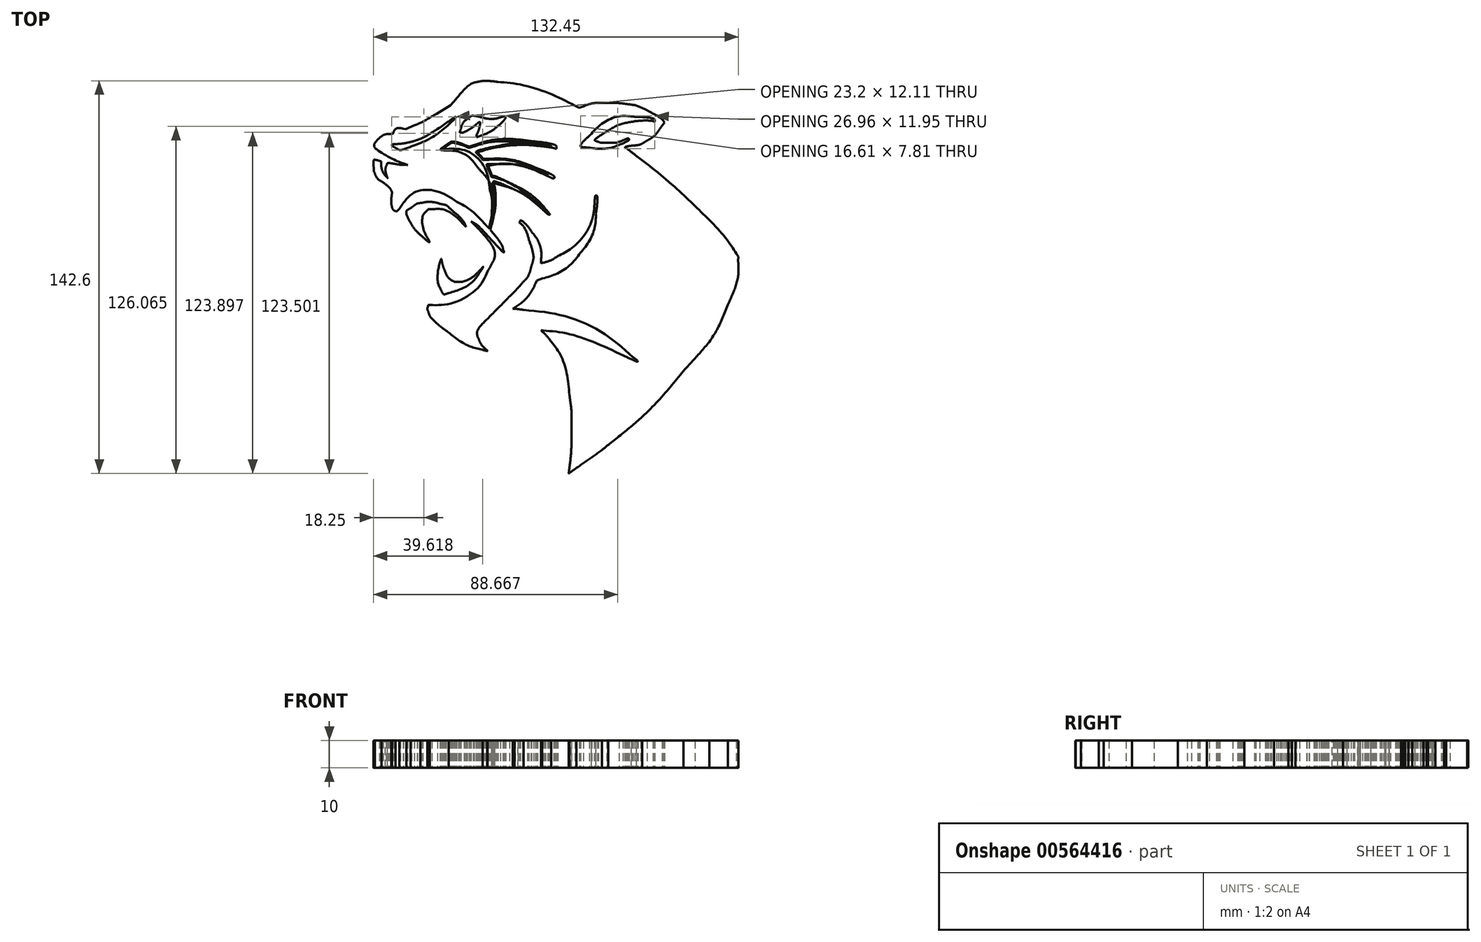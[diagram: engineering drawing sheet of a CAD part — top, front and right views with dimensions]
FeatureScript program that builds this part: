
annotation { "Feature Type Name" : "Feature", "Feature Type Description" : "" }
export const myFeature = defineFeature(function(context is Context, id is Id, definition is map)
    precondition{}
    {
        {
            var Q0;
            Q0=qCreatedBy(makeId("Top.planeOp"),FACE);
            var sketch = newSketch(context, id + "F0", { "sketchPlane" : qUnion([Q0])});
            skFitSpline(sketch, "E0", {"points": [v(4.12, -71.12) * mm, v(4.12, -70.9) * mm, v(4.21, -70) * mm, v(4.32, -69.1) * mm]});
            skFitSpline(sketch, "E1", {"points": [v(4.32, -69.1) * mm, v(5.26, -61.65) * mm, v(5.42, -52.29) * mm, v(4.74, -45.44) * mm]});
            skFitSpline(sketch, "E2", {"points": [v(4.74, -45.44) * mm, v(3.83, -36.4) * mm, v(1.7, -29.31) * mm, v(-1.62, -24.22) * mm]});
            skFitSpline(sketch, "E3", {"points": [v(-1.62, -24.22) * mm, v(-2.63, -22.67) * mm, v(-4.78, -20.17) * mm, v(-5.73, -19.43) * mm]});
            skFitSpline(sketch, "E4", {"points": [v(-5.73, -19.43) * mm, v(-6.02, -19.21) * mm, v(-6.25, -18.9) * mm, v(-6.25, -18.75) * mm]});
            skFitSpline(sketch, "E5", {"points": [v(-6.25, -18.75) * mm, v(-6.25, -18.44) * mm, v(-6.19, -18.44) * mm, v(-2.93, -18.9) * mm]});
            skFitSpline(sketch, "E6", {"points": [v(-2.93, -18.9) * mm, v(4, -19.85) * mm, v(14.69, -23.35) * mm, v(25.2, -28.1) * mm]});
            skFitSpline(sketch, "E7", {"points": [v(25.2, -28.1) * mm, v(26.49, -28.69) * mm, v(27.64, -29.2) * mm, v(27.75, -29.25) * mm]});
            skFitSpline(sketch, "E8", {"points": [v(27.75, -29.25) * mm, v(28.18, -29.42) * mm, v(23.73, -26.1) * mm, v(21.96, -24.93) * mm]});
            skFitSpline(sketch, "E9", {"points": [v(21.96, -24.93) * mm, v(11.21, -17.82) * mm, v(-2.37, -12.86) * mm, v(-14.52, -11.6) * mm]});
            skFitSpline(sketch, "E10", {"points": [v(-14.52, -11.6) * mm, v(-16.71, -11.38) * mm, v(-16.9, -11.24) * mm, v(-15.82, -10.6) * mm]});
            skFitSpline(sketch, "E11", {"points": [v(-15.82, -10.6) * mm, v(-13.27, -9.1) * mm, v(-9.35, -4.61) * mm, v(-7.78, -1.4) * mm]});
            skFitSpline(sketch, "E12", {"points": [v(-7.78, -1.4) * mm, v(-7.39, -0.6) * mm, v(-7.26, -0.46) * mm, v(-6.75, -0.31) * mm]});
            skFitSpline(sketch, "E13", {"points": [v(-6.75, -0.31) * mm, v(-4.24, 0.42) * mm, v(-0.38, 2.42) * mm, v(1.98, 4.23) * mm]});
            skFitSpline(sketch, "E14", {"points": [v(1.98, 4.23) * mm, v(9.16, 9.74) * mm, v(13.82, 18.08) * mm, v(14.15, 26.05) * mm]});
            skFitSpline(sketch, "E15", {"points": [v(13.87, 26.2) * mm, v(12.03, 18.53) * mm, v(6.27, 10.76) * mm, v(-0.37, 7) * mm]});
            skFitSpline(sketch, "E16", {"points": [v(-0.37, 7) * mm, v(-1.97, 6.1) * mm, v(-4.01, 5.3) * mm, v(-5.09, 5.16) * mm]});
            skLineSegment(sketch, "E17", {"start": v(14.15, 26.05) * mm, "end": v(14.22, 27.64) * mm});
            skLineSegment(sketch, "E18", {"start": v(14.22, 27.64) * mm, "end": v(13.87, 26.2) * mm});
            skFitSpline(sketch, "E19", {"points": [v(-5.83, 5.76) * mm, v(-5.83, 9.94) * mm, v(-7.3, 14.16) * mm, v(-9.82, 17.24) * mm]});
            skFitSpline(sketch, "E20", {"points": [v(-9.82, 17.24) * mm, v(-10.64, 18.24) * mm, v(-11.89, 19.44) * mm, v(-12.11, 19.44) * mm]});
            skFitSpline(sketch, "E21", {"points": [v(-12.11, 19.44) * mm, v(-12.17, 19.44) * mm, v(-12, 19.13) * mm, v(-11.74, 18.76) * mm]});
            skFitSpline(sketch, "E22", {"points": [v(-11.74, 18.76) * mm, v(-9.25, 15.2) * mm, v(-8.15, 8.63) * mm, v(-9.24, 3.9) * mm]});
            skFitSpline(sketch, "E23", {"points": [v(-9.24, 3.9) * mm, v(-9.57, 2.5) * mm, v(-10.53, 0.23) * mm, v(-11.3, -0.93) * mm]});
            skFitSpline(sketch, "E24", {"points": [v(-11.3, -0.93) * mm, v(-12.03, -2.05) * mm, v(-14.6, -4.79) * mm, v(-20.43, -10.68) * mm]});
            skFitSpline(sketch, "E25", {"points": [v(-20.43, -10.68) * mm, v(-25.1, -15.4) * mm, v(-27.6, -18.05) * mm, v(-27.91, -18.6) * mm]});
            skFitSpline(sketch, "E26", {"points": [v(-27.91, -18.6) * mm, v(-28.04, -18.82) * mm, v(-28.17, -19.43) * mm, v(-28.2, -20.02) * mm]});
            skFitSpline(sketch, "E27", {"points": [v(-28.2, -20.02) * mm, v(-28.25, -20.95) * mm, v(-28.2, -21.15) * mm, v(-27.74, -22.24) * mm]});
            skFitSpline(sketch, "E28", {"points": [v(-27.74, -22.24) * mm, v(-27.16, -23.6) * mm, v(-25.99, -25.08) * mm, v(-24.73, -26.04) * mm]});
            skFitSpline(sketch, "E29", {"points": [v(-24.73, -26.04) * mm, v(-24.3, -26.37) * mm, v(-23.94, -26.7) * mm, v(-23.94, -26.78) * mm]});
            skFitSpline(sketch, "E30", {"points": [v(-23.94, -26.78) * mm, v(-23.94, -27.37) * mm, v(-28.38, -26.2) * mm, v(-31.6, -24.76) * mm]});
            skFitSpline(sketch, "E31", {"points": [v(-31.6, -24.76) * mm, v(-33.32, -24) * mm, v(-36.75, -22.01) * mm, v(-38.31, -20.87) * mm]});
            skFitSpline(sketch, "E32", {"points": [v(-38.31, -20.87) * mm, v(-42.29, -17.96) * mm, v(-45.58, -14.42) * mm, v(-46.56, -12.02) * mm]});
            skFitSpline(sketch, "E33", {"points": [v(-46.56, -12.02) * mm, v(-46.91, -11.14) * mm, v(-47, -9.7) * mm, v(-46.7, -9.43) * mm]});
            skFitSpline(sketch, "E34", {"points": [v(-46.7, -9.43) * mm, v(-46.61, -9.35) * mm, v(-45.91, -9.24) * mm, v(-45.15, -9.2) * mm]});
            skFitSpline(sketch, "E35", {"points": [v(-45.15, -9.2) * mm, v(-40.65, -8.93) * mm, v(-34.12, -5.97) * mm, v(-29.58, -2.15) * mm]});
            skFitSpline(sketch, "E36", {"points": [v(-29.58, -2.15) * mm, v(-28.1, -0.9) * mm, v(-26.11, 1.39) * mm, v(-25.28, 2.8) * mm]});
            skFitSpline(sketch, "E37", {"points": [v(-25.28, 2.8) * mm, v(-22.36, 7.75) * mm, v(-24.01, 12.95) * mm, v(-30.64, 19.72) * mm]});
            skFitSpline(sketch, "E38", {"points": [v(-30.64, 19.72) * mm, v(-31.44, 20.54) * mm, v(-31.7, 20.9) * mm, v(-31.6, 21.03) * mm]});
            skFitSpline(sketch, "E39", {"points": [v(-31.6, 21.03) * mm, v(-31.38, 21.28) * mm, v(-30.28, 20.82) * mm, v(-29.2, 20) * mm]});
            skFitSpline(sketch, "E40", {"points": [v(-29.2, 20) * mm, v(-28, 19.11) * mm, v(-26.82, 17.97) * mm, v(-23.58, 14.52) * mm]});
            skFitSpline(sketch, "E41", {"points": [v(-23.58, 14.52) * mm, v(-22.08, 12.93) * mm, v(-20.62, 11.4) * mm, v(-20.32, 11.13) * mm]});
            skLineSegment(sketch, "E42", {"start": v(-5.09, 5.16) * mm, "end": v(-5.83, 5.06) * mm});
            skLineSegment(sketch, "E43", {"start": v(-5.83, 5.06) * mm, "end": v(-5.83, 5.76) * mm});
            skFitSpline(sketch, "E44", {"points": [v(-20.21, 11.5) * mm, v(-21.27, 13.58) * mm, v(-23.88, 16.98) * mm, v(-26.22, 19.32) * mm]});
            skFitSpline(sketch, "E45", {"points": [v(-26.22, 19.32) * mm, v(-27.27, 20.37) * mm, v(-29.86, 22.55) * mm, v(-31.29, 23.58) * mm]});
            skFitSpline(sketch, "E46", {"points": [v(-31.29, 23.58) * mm, v(-41.27, 30.8) * mm, v(-51.02, 31.4) * mm, v(-57.07, 25.13) * mm]});
            skFitSpline(sketch, "E47", {"points": [v(-57.07, 25.13) * mm, v(-57.88, 24.29) * mm, v(-57.96, 24.24) * mm, v(-58.38, 24.38) * mm]});
            skFitSpline(sketch, "E48", {"points": [v(-58.38, 24.38) * mm, v(-58.96, 24.57) * mm, v(-59.54, 25.3) * mm, v(-59.73, 26.08) * mm]});
            skFitSpline(sketch, "E49", {"points": [v(-59.73, 26.08) * mm, v(-59.9, 26.77) * mm, v(-59.9, 29.14) * mm, v(-59.75, 30.4) * mm]});
            skFitSpline(sketch, "E50", {"points": [v(-59.75, 30.4) * mm, v(-59.67, 31.05) * mm, v(-59.7, 31.33) * mm, v(-59.88, 31.67) * mm]});
            skFitSpline(sketch, "E51", {"points": [v(-59.88, 31.67) * mm, v(-60.31, 32.5) * mm, v(-62.06, 34.15) * mm, v(-63.53, 35.12) * mm]});
            skFitSpline(sketch, "E52", {"points": [v(-63.53, 35.12) * mm, v(-64.59, 35.83) * mm, v(-65.36, 36.75) * mm, v(-65.84, 37.88) * mm]});
            skFitSpline(sketch, "E53", {"points": [v(-65.84, 37.88) * mm, v(-66.21, 38.74) * mm, v(-66.3, 39.14) * mm, v(-66.34, 40.28) * mm]});
            skFitSpline(sketch, "E54", {"points": [v(-66.34, 40.28) * mm, v(-66.4, 41.8) * mm, v(-66.2, 43.01) * mm, v(-65.88, 43.01) * mm]});
            skFitSpline(sketch, "E55", {"points": [v(-65.88, 43.01) * mm, v(-65.77, 43.01) * mm, v(-65.22, 42.9) * mm, v(-64.65, 42.75) * mm]});
            skLineSegment(sketch, "E56", {"start": v(-20.32, 11.13) * mm, "end": v(-19.78, 10.64) * mm});
            skLineSegment(sketch, "E57", {"start": v(-19.78, 10.64) * mm, "end": v(-20.21, 11.5) * mm});
            skFitSpline(sketch, "E58", {"points": [v(-63.6, 41.83) * mm, v(-63.6, 40.8) * mm, v(-63.23, 39.05) * mm, v(-62.86, 38.34) * mm]});
            skFitSpline(sketch, "E59", {"points": [v(-62.86, 38.34) * mm, v(-62.67, 37.97) * mm, v(-62.22, 37.35) * mm, v(-61.86, 36.96) * mm]});
            skFitSpline(sketch, "E60", {"points": [v(-61.86, 36.96) * mm, v(-61.5, 36.57) * mm, v(-61.27, 36.35) * mm, v(-61.35, 36.48) * mm]});
            skFitSpline(sketch, "E61", {"points": [v(-61.35, 36.48) * mm, v(-61.44, 36.61) * mm, v(-61.61, 37.15) * mm, v(-61.74, 37.67) * mm]});
            skFitSpline(sketch, "E62", {"points": [v(-61.74, 37.67) * mm, v(-62.03, 38.8) * mm, v(-61.96, 40.31) * mm, v(-61.58, 41.2) * mm]});
            skFitSpline(sketch, "E63", {"points": [v(-61.58, 41.2) * mm, v(-61.34, 41.77) * mm, v(-61.28, 41.82) * mm, v(-60.77, 41.8) * mm]});
            skFitSpline(sketch, "E64", {"points": [v(-60.77, 41.8) * mm, v(-60.47, 41.79) * mm, v(-59.54, 41.66) * mm, v(-58.7, 41.51) * mm]});
            skFitSpline(sketch, "E65", {"points": [v(-58.7, 41.51) * mm, v(-57.87, 41.37) * mm, v(-56.47, 41.2) * mm, v(-55.6, 41.16) * mm]});
            skLineSegment(sketch, "E66", {"start": v(-64.65, 42.75) * mm, "end": v(-63.6, 42.49) * mm});
            skLineSegment(sketch, "E67", {"start": v(-63.6, 42.49) * mm, "end": v(-63.6, 41.83) * mm});
            skFitSpline(sketch, "E68", {"points": [v(-55.45, 41.65) * mm, v(-58.45, 42.84) * mm, v(-66.1, 47.59) * mm, v(-66.1, 48.27) * mm]});
            skFitSpline(sketch, "E69", {"points": [v(-66.1, 48.27) * mm, v(-66.1, 48.73) * mm, v(-65.08, 50.16) * mm, v(-64.2, 50.91) * mm]});
            skFitSpline(sketch, "E70", {"points": [v(-64.2, 50.91) * mm, v(-63.17, 51.8) * mm, v(-62.04, 52.26) * mm, v(-60.55, 52.37) * mm]});
            skFitSpline(sketch, "E71", {"points": [v(-60.55, 52.37) * mm, v(-59.37, 52.45) * mm, v(-59.36, 52.46) * mm, v(-59.11, 53) * mm]});
            skFitSpline(sketch, "E72", {"points": [v(-59.11, 53) * mm, v(-58.6, 54.08) * mm, v(-57.28, 54.57) * mm, v(-55.58, 54.3) * mm]});
            skLineSegment(sketch, "E73", {"start": v(-55.6, 41.16) * mm, "end": v(-54, 41.08) * mm});
            skLineSegment(sketch, "E74", {"start": v(-54, 41.08) * mm, "end": v(-55.45, 41.65) * mm});
            skFitSpline(sketch, "E75", {"points": [v(-51.52, 55.5) * mm, v(-48.89, 56.64) * mm, v(-47.57, 57.34) * mm, v(-43.43, 59.8) * mm]});
            skLineSegment(sketch, "E76", {"start": v(-55.58, 54.3) * mm, "end": v(-54.67, 54.15) * mm});
            skLineSegment(sketch, "E77", {"start": v(-54.67, 54.15) * mm, "end": v(-51.52, 55.5) * mm});
            skFitSpline(sketch, "E78", {"points": [v(-36.5, 65.02) * mm, v(-33.33, 68.67) * mm, v(-30.66, 70.77) * mm, v(-28.52, 71.3) * mm]});
            skFitSpline(sketch, "E79", {"points": [v(-28.52, 71.3) * mm, v(-27.3, 71.6) * mm, v(-23.84, 71.6) * mm, v(-21.23, 71.29) * mm]});
            skFitSpline(sketch, "E80", {"points": [v(-21.23, 71.29) * mm, v(-13.16, 70.36) * mm, v(-2.64, 67.12) * mm, v(6.75, 62.7) * mm]});
            skLineSegment(sketch, "E81", {"start": v(-43.43, 59.8) * mm, "end": v(-38.47, 62.73) * mm});
            skLineSegment(sketch, "E82", {"start": v(-38.47, 62.73) * mm, "end": v(-36.5, 65.02) * mm});
            skFitSpline(sketch, "E83", {"points": [v(9.78, 62.43) * mm, v(12.76, 63.43) * mm, v(14.24, 63.63) * mm, v(18.77, 63.64) * mm]});
            skFitSpline(sketch, "E84", {"points": [v(18.77, 63.64) * mm, v(21.4, 63.64) * mm, v(23.31, 63.57) * mm, v(24.16, 63.43) * mm]});
            skFitSpline(sketch, "E85", {"points": [v(24.16, 63.43) * mm, v(30.95, 62.35) * mm, v(36.33, 60.2) * mm, v(38.99, 57.52) * mm]});
            skFitSpline(sketch, "E86", {"points": [v(38.99, 57.52) * mm, v(39.69, 56.8) * mm, v(39.65, 56.45) * mm, v(38.77, 55.34) * mm]});
            skFitSpline(sketch, "E87", {"points": [v(38.77, 55.34) * mm, v(36.9, 52.94) * mm, v(35.05, 51.27) * mm, v(32.87, 49.96) * mm]});
            skFitSpline(sketch, "E88", {"points": [v(32.87, 49.96) * mm, v(30.67, 48.64) * mm, v(28.73, 47.92) * mm, v(26.46, 47.56) * mm]});
            skLineSegment(sketch, "E89", {"start": v(6.75, 62.7) * mm, "end": v(8.32, 61.95) * mm});
            skLineSegment(sketch, "E90", {"start": v(8.32, 61.95) * mm, "end": v(9.78, 62.43) * mm});
            skFitSpline(sketch, "E91", {"points": [v(28.68, 45.2) * mm, v(38.35, 37.67) * mm, v(46.63, 30.45) * mm, v(53.44, 23.6) * mm]});
            skFitSpline(sketch, "E92", {"points": [v(53.44, 23.6) * mm, v(57.8, 19.21) * mm, v(63.61, 12.27) * mm, v(65.81, 8.8) * mm]});
            skLineSegment(sketch, "E93", {"start": v(26.46, 47.56) * mm, "end": v(25.8, 47.45) * mm});
            skLineSegment(sketch, "E94", {"start": v(25.8, 47.45) * mm, "end": v(28.68, 45.2) * mm});
            skFitSpline(sketch, "E95", {"points": [v(66.27, 6.16) * mm, v(66.03, 1.2) * mm, v(64.77, -3.75) * mm, v(62.24, -9.63) * mm]});
            skFitSpline(sketch, "E96", {"points": [v(62.24, -9.63) * mm, v(58.63, -18) * mm, v(53.53, -25.72) * mm, v(45.3, -35.2) * mm]});
            skFitSpline(sketch, "E97", {"points": [v(45.3, -35.2) * mm, v(37.81, -43.86) * mm, v(29.25, -52.05) * mm, v(18.77, -60.6) * mm]});
            skFitSpline(sketch, "E98", {"points": [v(18.77, -60.6) * mm, v(13.89, -64.58) * mm, v(4.67, -71.52) * mm, v(4.26, -71.52) * mm]});
            skFitSpline(sketch, "E99", {"points": [v(4.26, -71.52) * mm, v(4.18, -71.52) * mm, v(4.12, -71.34) * mm, v(4.12, -71.12) * mm]});
            skLineSegment(sketch, "E100", {"start": v(65.81, 8.8) * mm, "end": v(66.35, 7.94) * mm});
            skLineSegment(sketch, "E101", {"start": v(66.35, 7.94) * mm, "end": v(66.27, 6.16) * mm});
            skFitSpline(sketch, "E102", {"points": [v(7.3, -68.92) * mm, v(21.83, -58.41) * mm, v(35.94, -45.62) * mm, v(46.07, -33.74) * mm]});
            skFitSpline(sketch, "E103", {"points": [v(46.07, -33.74) * mm, v(58.55, -19.12) * mm, v(65.22, -5.67) * mm, v(65.97, 6.38) * mm]});
            skFitSpline(sketch, "E104", {"points": [v(65.26, 8.92) * mm, v(62.17, 13.59) * mm, v(56.38, 20.25) * mm, v(50.27, 26.16) * mm]});
            skFitSpline(sketch, "E105", {"points": [v(50.27, 26.16) * mm, v(44.57, 31.66) * mm, v(36.74, 38.38) * mm, v(28.75, 44.63) * mm]});
            skFitSpline(sketch, "E106", {"points": [v(28.75, 44.63) * mm, v(26.95, 46.04) * mm, v(25.4, 47.23) * mm, v(25.3, 47.27) * mm]});
            skFitSpline(sketch, "E107", {"points": [v(25.3, 47.27) * mm, v(24.96, 47.42) * mm, v(25.13, 47.78) * mm, v(25.57, 47.85) * mm]});
            skFitSpline(sketch, "E108", {"points": [v(25.57, 47.85) * mm, v(25.82, 47.9) * mm, v(26.52, 48.01) * mm, v(27.13, 48.11) * mm]});
            skFitSpline(sketch, "E109", {"points": [v(27.13, 48.11) * mm, v(31, 48.75) * mm, v(35.54, 51.72) * mm, v(38.36, 55.46) * mm]});
            skLineSegment(sketch, "E110", {"start": v(65.97, 6.38) * mm, "end": v(66.05, 7.73) * mm});
            skLineSegment(sketch, "E111", {"start": v(66.05, 7.73) * mm, "end": v(65.26, 8.92) * mm});
            skFitSpline(sketch, "E112", {"points": [v(38.85, 57.07) * mm, v(38.27, 57.76) * mm, v(36.42, 59.08) * mm, v(35.08, 59.75) * mm]});
            skFitSpline(sketch, "E113", {"points": [v(35.08, 59.75) * mm, v(29.66, 62.46) * mm, v(21.89, 63.86) * mm, v(15.73, 63.24) * mm]});
            skFitSpline(sketch, "E114", {"points": [v(15.73, 63.24) * mm, v(13.63, 63.03) * mm, v(11.42, 62.57) * mm, v(9.7, 61.98) * mm]});
            skLineSegment(sketch, "E115", {"start": v(38.36, 55.46) * mm, "end": v(39.23, 56.61) * mm});
            skLineSegment(sketch, "E116", {"start": v(39.23, 56.61) * mm, "end": v(38.85, 57.07) * mm});
            skFitSpline(sketch, "E117", {"points": [v(6.25, 62.46) * mm, v(-2.23, 66.4) * mm, v(-11.3, 69.32) * mm, v(-18.9, 70.56) * mm]});
            skFitSpline(sketch, "E118", {"points": [v(-18.9, 70.56) * mm, v(-23.14, 71.25) * mm, v(-27.04, 71.36) * mm, v(-28.7, 70.83) * mm]});
            skFitSpline(sketch, "E119", {"points": [v(-28.7, 70.83) * mm, v(-30.9, 70.13) * mm, v(-33.14, 68.28) * mm, v(-36.35, 64.56) * mm]});
            skLineSegment(sketch, "E120", {"start": v(9.7, 61.98) * mm, "end": v(8.32, 61.5) * mm});
            skLineSegment(sketch, "E121", {"start": v(8.32, 61.5) * mm, "end": v(6.25, 62.46) * mm});
            skFitSpline(sketch, "E122", {"points": [v(-43.26, 59.42) * mm, v(-47.6, 56.85) * mm, v(-48.8, 56.22) * mm, v(-51.54, 55.05) * mm]});
            skFitSpline(sketch, "E123", {"points": [v(-51.54, 55.05) * mm, v(-54.68, 53.7) * mm, v(-54.76, 53.68) * mm, v(-55.38, 53.86) * mm]});
            skFitSpline(sketch, "E124", {"points": [v(-55.38, 53.86) * mm, v(-56.25, 54.11) * mm, v(-57.54, 53.96) * mm, v(-58.15, 53.53) * mm]});
            skFitSpline(sketch, "E125", {"points": [v(-58.15, 53.53) * mm, v(-58.42, 53.33) * mm, v(-58.75, 52.92) * mm, v(-58.9, 52.6) * mm]});
            skLineSegment(sketch, "E126", {"start": v(-36.35, 64.56) * mm, "end": v(-38.2, 62.42) * mm});
            skLineSegment(sketch, "E127", {"start": v(-38.2, 62.42) * mm, "end": v(-43.26, 59.42) * mm});
            skFitSpline(sketch, "E128", {"points": [v(-60.25, 51.99) * mm, v(-62.22, 51.93) * mm, v(-64.02, 50.95) * mm, v(-65.12, 49.35) * mm]});
            skFitSpline(sketch, "E129", {"points": [v(-65.12, 49.35) * mm, v(-65.43, 48.9) * mm, v(-65.68, 48.46) * mm, v(-65.68, 48.36) * mm]});
            skFitSpline(sketch, "E130", {"points": [v(-65.68, 48.36) * mm, v(-65.68, 48.13) * mm, v(-61.72, 45.42) * mm, v(-59.67, 44.24) * mm]});
            skFitSpline(sketch, "E131", {"points": [v(-59.67, 44.24) * mm, v(-56.75, 42.57) * mm, v(-53.66, 41.26) * mm, v(-52.6, 41.26) * mm]});
            skFitSpline(sketch, "E132", {"points": [v(-52.6, 41.26) * mm, v(-52.44, 41.26) * mm, v(-52.32, 41.16) * mm, v(-52.32, 41.03) * mm]});
            skFitSpline(sketch, "E133", {"points": [v(-52.32, 41.03) * mm, v(-52.32, 40.52) * mm, v(-54.93, 40.52) * mm, v(-58.28, 41.04) * mm]});
            skFitSpline(sketch, "E134", {"points": [v(-58.28, 41.04) * mm, v(-61.43, 41.52) * mm, v(-61.07, 41.55) * mm, v(-61.33, 40.84) * mm]});
            skFitSpline(sketch, "E135", {"points": [v(-61.33, 40.84) * mm, v(-61.68, 39.88) * mm, v(-61.56, 37.88) * mm, v(-61.07, 36.89) * mm]});
            skFitSpline(sketch, "E136", {"points": [v(-61.07, 36.89) * mm, v(-60.45, 35.6) * mm, v(-60.65, 35.33) * mm, v(-61.62, 36.14) * mm]});
            skFitSpline(sketch, "E137", {"points": [v(-61.62, 36.14) * mm, v(-63, 37.29) * mm, v(-63.73, 38.88) * mm, v(-63.85, 40.96) * mm]});
            skLineSegment(sketch, "E138", {"start": v(-58.9, 52.6) * mm, "end": v(-59.15, 52.02) * mm});
            skLineSegment(sketch, "E139", {"start": v(-59.15, 52.02) * mm, "end": v(-60.25, 51.99) * mm});
            skFitSpline(sketch, "E140", {"points": [v(-64.8, 42.37) * mm, v(-65.49, 42.53) * mm, v(-65.74, 42.53) * mm, v(-65.86, 42.39) * mm]});
            skFitSpline(sketch, "E141", {"points": [v(-65.86, 42.39) * mm, v(-65.96, 42.27) * mm, v(-66.02, 41.64) * mm, v(-66.02, 40.73) * mm]});
            skFitSpline(sketch, "E142", {"points": [v(-66.02, 40.73) * mm, v(-66.02, 39.4) * mm, v(-65.98, 39.17) * mm, v(-65.57, 38.2) * mm]});
            skFitSpline(sketch, "E143", {"points": [v(-65.57, 38.2) * mm, v(-65.1, 37.11) * mm, v(-64.1, 35.9) * mm, v(-63.27, 35.42) * mm]});
            skFitSpline(sketch, "E144", {"points": [v(-63.27, 35.42) * mm, v(-62.6, 35.02) * mm, v(-61.11, 33.77) * mm, v(-60.38, 32.99) * mm]});
            skFitSpline(sketch, "E145", {"points": [v(-60.38, 32.99) * mm, v(-59.33, 31.86) * mm, v(-59.27, 31.66) * mm, v(-59.46, 29.61) * mm]});
            skFitSpline(sketch, "E146", {"points": [v(-59.46, 29.61) * mm, v(-59.69, 27.15) * mm, v(-59.47, 25.8) * mm, v(-58.75, 25.1) * mm]});
            skFitSpline(sketch, "E147", {"points": [v(-58.75, 25.1) * mm, v(-58.52, 24.88) * mm, v(-58.26, 24.7) * mm, v(-58.16, 24.7) * mm]});
            skFitSpline(sketch, "E148", {"points": [v(-58.16, 24.7) * mm, v(-58.07, 24.7) * mm, v(-57.62, 25.1) * mm, v(-57.17, 25.58) * mm]});
            skFitSpline(sketch, "E149", {"points": [v(-57.17, 25.58) * mm, v(-55.58, 27.29) * mm, v(-53.36, 28.6) * mm, v(-50.81, 29.35) * mm]});
            skFitSpline(sketch, "E150", {"points": [v(-50.81, 29.35) * mm, v(-49.72, 29.67) * mm, v(-49.24, 29.7) * mm, v(-46.6, 29.7) * mm]});
            skFitSpline(sketch, "E151", {"points": [v(-46.6, 29.7) * mm, v(-44.04, 29.7) * mm, v(-43.44, 29.65) * mm, v(-42.18, 29.34) * mm]});
            skFitSpline(sketch, "E152", {"points": [v(-42.18, 29.34) * mm, v(-36.75, 27.98) * mm, v(-30.57, 24.23) * mm, v(-25.64, 19.3) * mm]});
            skFitSpline(sketch, "E153", {"points": [v(-25.64, 19.3) * mm, v(-25.02, 18.67) * mm, v(-24.48, 18.16) * mm, v(-24.45, 18.16) * mm]});
            skFitSpline(sketch, "E154", {"points": [v(-24.45, 18.16) * mm, v(-24.41, 18.16) * mm, v(-24.28, 18.8) * mm, v(-24.16, 19.56) * mm]});
            skFitSpline(sketch, "E155", {"points": [v(-24.16, 19.56) * mm, v(-22.86, 27.94) * mm, v(-24.33, 34.93) * mm, v(-28.46, 40) * mm]});
            skFitSpline(sketch, "E156", {"points": [v(-28.46, 40) * mm, v(-31.58, 43.82) * mm, v(-35.76, 46) * mm, v(-40.83, 46.45) * mm]});
            skFitSpline(sketch, "E157", {"points": [v(-40.83, 46.45) * mm, v(-41.66, 46.53) * mm, v(-42.04, 46.62) * mm, v(-42.04, 46.76) * mm]});
            skFitSpline(sketch, "E158", {"points": [v(-42.04, 46.76) * mm, v(-42.04, 46.87) * mm, v(-41.21, 47.54) * mm, v(-40.2, 48.25) * mm]});
            skFitSpline(sketch, "E159", {"points": [v(-40.2, 48.25) * mm, v(-38.76, 49.26) * mm, v(-38.23, 49.54) * mm, v(-37.83, 49.54) * mm]});
            skFitSpline(sketch, "E160", {"points": [v(-37.83, 49.54) * mm, v(-37, 49.54) * mm, v(-34.63, 48.94) * mm, v(-33.08, 48.33) * mm]});
            skLineSegment(sketch, "E161", {"start": v(-63.85, 40.96) * mm, "end": v(-63.91, 42.17) * mm});
            skLineSegment(sketch, "E162", {"start": v(-63.91, 42.17) * mm, "end": v(-64.8, 42.37) * mm});
            skFitSpline(sketch, "E163", {"points": [v(-30.04, 48.25) * mm, v(-24.16, 50) * mm, v(-16.45, 50.57) * mm, v(-9.22, 49.78) * mm]});
            skFitSpline(sketch, "E164", {"points": [v(-9.22, 49.78) * mm, v(-4.56, 49.27) * mm, v(-0.03, 48) * mm, v(-0.03, 47.22) * mm]});
            skFitSpline(sketch, "E165", {"points": [v(-0.03, 47.22) * mm, v(-0.03, 47.03) * mm, v(-0.1, 46.98) * mm, v(-0.34, 47.06) * mm]});
            skFitSpline(sketch, "E166", {"points": [v(-0.34, 47.06) * mm, v(-1.02, 47.27) * mm, v(-5.47, 47.94) * mm, v(-7.4, 48.12) * mm]});
            skFitSpline(sketch, "E167", {"points": [v(-7.4, 48.12) * mm, v(-10.02, 48.36) * mm, v(-16.85, 48.22) * mm, v(-19.24, 47.88) * mm]});
            skFitSpline(sketch, "E168", {"points": [v(-19.24, 47.88) * mm, v(-22.4, 47.42) * mm, v(-24.93, 46.86) * mm, v(-27.35, 46.09) * mm]});
            skLineSegment(sketch, "E169", {"start": v(-33.08, 48.33) * mm, "end": v(-31.66, 47.77) * mm});
            skLineSegment(sketch, "E170", {"start": v(-31.66, 47.77) * mm, "end": v(-30.04, 48.25) * mm});
            skFitSpline(sketch, "E171", {"points": [v(-23.81, 43.38) * mm, v(-18.53, 43.33) * mm, v(-12.84, 42.18) * mm, v(-7.35, 40.05) * mm]});
            skFitSpline(sketch, "E172", {"points": [v(-7.35, 40.05) * mm, v(-3.86, 38.69) * mm, v(-0.6, 36.72) * mm, v(-1.04, 36.22) * mm]});
            skFitSpline(sketch, "E173", {"points": [v(-1.04, 36.22) * mm, v(-1.08, 36.17) * mm, v(-1.97, 36.51) * mm, v(-3.02, 36.97) * mm]});
            skFitSpline(sketch, "E174", {"points": [v(-3.02, 36.97) * mm, v(-9.99, 40.02) * mm, v(-18.3, 41.61) * mm, v(-23.97, 41) * mm]});
            skLineSegment(sketch, "E175", {"start": v(-27.35, 46.09) * mm, "end": v(-28.63, 45.68) * mm});
            skLineSegment(sketch, "E176", {"start": v(-28.63, 45.68) * mm, "end": v(-27.57, 44.55) * mm});
            skLineSegment(sketch, "E177", {"start": v(-27.57, 44.55) * mm, "end": v(-26.52, 43.41) * mm});
            skLineSegment(sketch, "E178", {"start": v(-26.52, 43.41) * mm, "end": v(-23.81, 43.38) * mm});
            skFitSpline(sketch, "E179", {"points": [v(-24.52, 40.08) * mm, v(-24.3, 39.64) * mm, v(-23.95, 38.79) * mm, v(-23.74, 38.2) * mm]});
            skFitSpline(sketch, "E180", {"points": [v(-23.74, 38.2) * mm, v(-23.48, 37.5) * mm, v(-23.26, 37.12) * mm, v(-23.12, 37.12) * mm]});
            skFitSpline(sketch, "E181", {"points": [v(-23.12, 37.12) * mm, v(-22.68, 37.11) * mm, v(-18.84, 35.54) * mm, v(-16.97, 34.59) * mm]});
            skFitSpline(sketch, "E182", {"points": [v(-16.97, 34.59) * mm, v(-11.9, 32.03) * mm, v(-6.68, 28.2) * mm, v(-3.86, 24.99) * mm]});
            skFitSpline(sketch, "E183", {"points": [v(-3.86, 24.99) * mm, v(-2.76, 23.74) * mm, v(-2.4, 23.1) * mm, v(-2.8, 23.1) * mm]});
            skFitSpline(sketch, "E184", {"points": [v(-2.8, 23.1) * mm, v(-2.88, 23.1) * mm, v(-3.77, 23.8) * mm, v(-4.77, 24.67) * mm]});
            skFitSpline(sketch, "E185", {"points": [v(-4.77, 24.67) * mm, v(-9.79, 29) * mm, v(-15.67, 32.38) * mm, v(-21.16, 34.07) * mm]});
            skLineSegment(sketch, "E186", {"start": v(-23.97, 41) * mm, "end": v(-24.9, 40.9) * mm});
            skLineSegment(sketch, "E187", {"start": v(-24.9, 40.9) * mm, "end": v(-24.52, 40.08) * mm});
            skFitSpline(sketch, "E188", {"points": [v(-22.65, 34.12) * mm, v(-22.13, 31.11) * mm, v(-22.18, 25.84) * mm, v(-22.76, 22.62) * mm]});
            skFitSpline(sketch, "E189", {"points": [v(-22.76, 22.62) * mm, v(-22.95, 21.53) * mm, v(-23.3, 19.93) * mm, v(-23.54, 19.08) * mm]});
            skLineSegment(sketch, "E190", {"start": v(-21.16, 34.07) * mm, "end": v(-22.73, 34.56) * mm});
            skLineSegment(sketch, "E191", {"start": v(-22.73, 34.56) * mm, "end": v(-22.65, 34.12) * mm});
            skFitSpline(sketch, "E192", {"points": [v(-22.95, 16.29) * mm, v(-21.32, 14.32) * mm, v(-19.65, 11.6) * mm, v(-19.37, 10.48) * mm]});
            skFitSpline(sketch, "E193", {"points": [v(-19.37, 10.48) * mm, v(-19.08, 9.34) * mm, v(-20.25, 10.33) * mm, v(-24.17, 14.55) * mm]});
            skFitSpline(sketch, "E194", {"points": [v(-24.17, 14.55) * mm, v(-27.04, 17.64) * mm, v(-28.87, 19.36) * mm, v(-30.06, 20.08) * mm]});
            skLineSegment(sketch, "E195", {"start": v(-23.54, 19.08) * mm, "end": v(-23.97, 17.52) * mm});
            skLineSegment(sketch, "E196", {"start": v(-23.97, 17.52) * mm, "end": v(-22.95, 16.29) * mm});
            skFitSpline(sketch, "E197", {"points": [v(-29.88, 19.51) * mm, v(-26.67, 16.13) * mm, v(-24.91, 13.49) * mm, v(-24, 10.68) * mm]});
            skFitSpline(sketch, "E198", {"points": [v(-24, 10.68) * mm, v(-23.66, 9.64) * mm, v(-23.6, 9.25) * mm, v(-23.6, 7.73) * mm]});
            skFitSpline(sketch, "E199", {"points": [v(-23.6, 7.73) * mm, v(-23.6, 5.61) * mm, v(-23.9, 4.36) * mm, v(-24.87, 2.73) * mm]});
            skFitSpline(sketch, "E200", {"points": [v(-24.87, 2.73) * mm, v(-28.65, -3.64) * mm, v(-37.9, -9.1) * mm, v(-46.05, -9.75) * mm]});
            skFitSpline(sketch, "E201", {"points": [v(-46.05, -9.75) * mm, v(-46.45, -9.78) * mm, v(-46.54, -9.86) * mm, v(-46.58, -10.18) * mm]});
            skFitSpline(sketch, "E202", {"points": [v(-46.58, -10.18) * mm, v(-46.82, -12.15) * mm, v(-43.6, -16.27) * mm, v(-39.13, -19.72) * mm]});
            skFitSpline(sketch, "E203", {"points": [v(-39.13, -19.72) * mm, v(-35.22, -22.73) * mm, v(-30.9, -24.94) * mm, v(-26.8, -26.04) * mm]});
            skFitSpline(sketch, "E204", {"points": [v(-26.8, -26.04) * mm, v(-25.9, -26.28) * mm, v(-25.14, -26.44) * mm, v(-25.1, -26.4) * mm]});
            skFitSpline(sketch, "E205", {"points": [v(-25.1, -26.4) * mm, v(-25.06, -26.36) * mm, v(-25.35, -26.04) * mm, v(-25.74, -25.7) * mm]});
            skFitSpline(sketch, "E206", {"points": [v(-25.74, -25.7) * mm, v(-26.7, -24.87) * mm, v(-27.62, -23.55) * mm, v(-28.14, -22.3) * mm]});
            skFitSpline(sketch, "E207", {"points": [v(-28.14, -22.3) * mm, v(-28.7, -20.94) * mm, v(-28.75, -19.36) * mm, v(-28.25, -18.44) * mm]});
            skFitSpline(sketch, "E208", {"points": [v(-28.25, -18.44) * mm, v(-27.88, -17.76) * mm, v(-25.9, -15.64) * mm, v(-21.32, -11.01) * mm]});
            skFitSpline(sketch, "E209", {"points": [v(-21.32, -11.01) * mm, v(-16.84, -6.49) * mm, v(-12.92, -2.4) * mm, v(-12.26, -1.57) * mm]});
            skFitSpline(sketch, "E210", {"points": [v(-12.26, -1.57) * mm, v(-9.18, 2.3) * mm, v(-8.34, 8.07) * mm, v(-10, 13.93) * mm]});
            skFitSpline(sketch, "E211", {"points": [v(-10, 13.93) * mm, v(-10.66, 16.26) * mm, v(-12.01, 18.88) * mm, v(-13.04, 19.8) * mm]});
            skFitSpline(sketch, "E212", {"points": [v(-13.04, 19.8) * mm, v(-13.33, 20.06) * mm, v(-13.4, 20.22) * mm, v(-13.3, 20.4) * mm]});
            skFitSpline(sketch, "E213", {"points": [v(-13.3, 20.4) * mm, v(-12.99, 20.96) * mm, v(-10.49, 18.89) * mm, v(-8.98, 16.82) * mm]});
            skFitSpline(sketch, "E214", {"points": [v(-8.98, 16.82) * mm, v(-6.89, 13.95) * mm, v(-5.56, 10.01) * mm, v(-5.56, 6.65) * mm]});
            skLineSegment(sketch, "E215", {"start": v(-30.06, 20.08) * mm, "end": v(-30.92, 20.6) * mm});
            skLineSegment(sketch, "E216", {"start": v(-30.92, 20.6) * mm, "end": v(-29.88, 19.51) * mm});
            skFitSpline(sketch, "E217", {"points": [v(-5.18, 5.51) * mm, v(-3.2, 6.02) * mm, v(-1.35, 6.83) * mm, v(0.46, 7.98) * mm]});
            skFitSpline(sketch, "E218", {"points": [v(0.46, 7.98) * mm, v(7.22, 12.3) * mm, v(12.8, 20.72) * mm, v(13.86, 28.2) * mm]});
            skFitSpline(sketch, "E219", {"points": [v(13.86, 28.2) * mm, v(13.97, 29.03) * mm, v(14.07, 29.77) * mm, v(14.07, 29.83) * mm]});
            skFitSpline(sketch, "E220", {"points": [v(14.07, 29.83) * mm, v(14.07, 29.9) * mm, v(14.15, 29.95) * mm, v(14.26, 29.95) * mm]});
            skFitSpline(sketch, "E221", {"points": [v(14.26, 29.95) * mm, v(14.7, 29.95) * mm, v(14.64, 25.5) * mm, v(14.14, 22.74) * mm]});
            skFitSpline(sketch, "E222", {"points": [v(14.14, 22.74) * mm, v(13.7, 20.27) * mm, v(12.58, 17.05) * mm, v(11.37, 14.74) * mm]});
            skFitSpline(sketch, "E223", {"points": [v(11.37, 14.74) * mm, v(7.8, 7.91) * mm, v(1.78, 2.46) * mm, v(-5.05, -0.13) * mm]});
            skLineSegment(sketch, "E224", {"start": v(-5.56, 6.65) * mm, "end": v(-5.56, 5.41) * mm});
            skLineSegment(sketch, "E225", {"start": v(-5.56, 5.41) * mm, "end": v(-5.18, 5.51) * mm});
            skFitSpline(sketch, "E226", {"points": [v(-7.65, -2) * mm, v(-9.15, -4.97) * mm, v(-12.42, -8.78) * mm, v(-15.02, -10.58) * mm]});
            skLineSegment(sketch, "E227", {"start": v(-5.05, -0.13) * mm, "end": v(-7.1, -0.9) * mm});
            skLineSegment(sketch, "E228", {"start": v(-7.1, -0.9) * mm, "end": v(-7.65, -2) * mm});
            skFitSpline(sketch, "E229", {"points": [v(-15.2, -11.15) * mm, v(-14.84, -11.15) * mm, v(-13.35, -11.32) * mm, v(-11.88, -11.54) * mm]});
            skFitSpline(sketch, "E230", {"points": [v(-11.88, -11.54) * mm, v(2.46, -13.64) * mm, v(16.86, -19.87) * mm, v(27.85, -28.72) * mm]});
            skFitSpline(sketch, "E231", {"points": [v(27.85, -28.72) * mm, v(29.14, -29.76) * mm, v(29.55, -30.26) * mm, v(29.1, -30.26) * mm]});
            skFitSpline(sketch, "E232", {"points": [v(29.1, -30.26) * mm, v(29.02, -30.26) * mm, v(27.54, -29.62) * mm, v(25.83, -28.84) * mm]});
            skFitSpline(sketch, "E233", {"points": [v(25.83, -28.84) * mm, v(13.85, -23.4) * mm, v(3.07, -19.94) * mm, v(-4.8, -19.03) * mm]});
            skLineSegment(sketch, "E234", {"start": v(-15.02, -10.58) * mm, "end": v(-15.84, -11.15) * mm});
            skLineSegment(sketch, "E235", {"start": v(-15.84, -11.15) * mm, "end": v(-15.2, -11.15) * mm});
            skFitSpline(sketch, "E236", {"points": [v(-5.14, -19.37) * mm, v(-4.29, -20.15) * mm, v(-2.65, -22.03) * mm, v(-1.9, -23.1) * mm]});
            skFitSpline(sketch, "E237", {"points": [v(-1.9, -23.1) * mm, v(1.42, -27.8) * mm, v(3.64, -34.26) * mm, v(4.73, -42.42) * mm]});
            skFitSpline(sketch, "E238", {"points": [v(4.73, -42.42) * mm, v(5.33, -46.91) * mm, v(5.43, -48.77) * mm, v(5.42, -55.19) * mm]});
            skFitSpline(sketch, "E239", {"points": [v(5.42, -55.19) * mm, v(5.42, -61.27) * mm, v(5.26, -64.26) * mm, v(4.73, -68.64) * mm]});
            skFitSpline(sketch, "E240", {"points": [v(4.73, -68.64) * mm, v(4.48, -70.7) * mm, v(4.48, -70.93) * mm, v(4.7, -70.78) * mm]});
            skFitSpline(sketch, "E241", {"points": [v(4.7, -70.78) * mm, v(4.8, -70.72) * mm, v(5.97, -69.88) * mm, v(7.3, -68.92) * mm]});
            skLineSegment(sketch, "E242", {"start": v(-4.8, -19.03) * mm, "end": v(-5.63, -18.93) * mm});
            skLineSegment(sketch, "E243", {"start": v(-5.63, -18.93) * mm, "end": v(-5.14, -19.37) * mm});
            skFitSpline(sketch, "E244", {"points": [v(-58.39, 47.32) * mm, v(-59.14, 47.76) * mm, v(-59.73, 48.21) * mm, v(-59.73, 48.34) * mm]});
            skFitSpline(sketch, "E245", {"points": [v(-59.73, 48.34) * mm, v(-59.73, 48.5) * mm, v(-59.5, 48.6) * mm, v(-58.94, 48.67) * mm]});
            skFitSpline(sketch, "E246", {"points": [v(-58.94, 48.67) * mm, v(-52.88, 49.44) * mm, v(-46.15, 52.32) * mm, v(-38.57, 57.37) * mm]});
            skFitSpline(sketch, "E247", {"points": [v(-38.57, 57.37) * mm, v(-37.54, 58.06) * mm, v(-36.66, 58.62) * mm, v(-36.63, 58.62) * mm]});
            skFitSpline(sketch, "E248", {"points": [v(-36.63, 58.62) * mm, v(-36.6, 58.62) * mm, v(-36.56, 58.5) * mm, v(-36.56, 58.37) * mm]});
            skFitSpline(sketch, "E249", {"points": [v(-36.56, 58.37) * mm, v(-36.56, 58.23) * mm, v(-37.16, 57.6) * mm, v(-37.9, 56.95) * mm]});
            skFitSpline(sketch, "E250", {"points": [v(-37.9, 56.95) * mm, v(-42.44, 52.99) * mm, v(-48, 49.7) * mm, v(-54.17, 47.32) * mm]});
            skFitSpline(sketch, "E251", {"points": [v(-54.17, 47.32) * mm, v(-55.32, 46.88) * mm, v(-56.44, 46.52) * mm, v(-56.65, 46.53) * mm]});
            skFitSpline(sketch, "E252", {"points": [v(-56.65, 46.53) * mm, v(-56.86, 46.53) * mm, v(-57.65, 46.89) * mm, v(-58.39, 47.32) * mm]});
            skFitSpline(sketch, "E253", {"points": [v(-54.41, 47.67) * mm, v(-50.5, 49.15) * mm, v(-46.08, 51.44) * mm, v(-42.73, 53.73) * mm]});
            skFitSpline(sketch, "E254", {"points": [v(-42.73, 53.73) * mm, v(-41.85, 54.33) * mm, v(-39.28, 56.27) * mm, v(-39.28, 56.33) * mm]});
            skFitSpline(sketch, "E255", {"points": [v(-39.28, 56.33) * mm, v(-39.28, 56.36) * mm, v(-39.86, 56.03) * mm, v(-40.56, 55.59) * mm]});
            skFitSpline(sketch, "E256", {"points": [v(-40.56, 55.59) * mm, v(-45.1, 52.72) * mm, v(-50.53, 50.2) * mm, v(-54.4, 49.15) * mm]});
            skFitSpline(sketch, "E257", {"points": [v(-54.4, 49.15) * mm, v(-55.6, 48.82) * mm, v(-58.34, 48.29) * mm, v(-58.92, 48.26) * mm]});
            skFitSpline(sketch, "E258", {"points": [v(-58.92, 48.26) * mm, v(-59.03, 48.26) * mm, v(-58.58, 47.94) * mm, v(-57.94, 47.56) * mm]});
            skFitSpline(sketch, "E259", {"points": [v(-57.94, 47.56) * mm, v(-56.6, 46.77) * mm, v(-56.81, 46.76) * mm, v(-54.41, 47.67) * mm]});
            skFitSpline(sketch, "E260", {"points": [v(12.55, 47.32) * mm, v(10, 47.56) * mm, v(8.82, 47.8) * mm, v(8.82, 48.06) * mm]});
            skFitSpline(sketch, "E261", {"points": [v(8.82, 48.06) * mm, v(8.82, 48.4) * mm, v(10.61, 50.5) * mm, v(12, 51.77) * mm]});
            skFitSpline(sketch, "E262", {"points": [v(12, 51.77) * mm, v(13.79, 53.42) * mm, v(15.34, 54.55) * mm, v(17.32, 55.67) * mm]});
            skFitSpline(sketch, "E263", {"points": [v(17.32, 55.67) * mm, v(21.26, 57.9) * mm, v(24.71, 58.75) * mm, v(29.13, 58.58) * mm]});
            skFitSpline(sketch, "E264", {"points": [v(29.13, 58.58) * mm, v(32.24, 58.46) * mm, v(35.64, 57.71) * mm, v(35.7, 57.14) * mm]});
            skFitSpline(sketch, "E265", {"points": [v(35.7, 57.14) * mm, v(35.74, 56.9) * mm, v(35.67, 56.88) * mm, v(35.24, 56.98) * mm]});
            skFitSpline(sketch, "E266", {"points": [v(35.24, 56.98) * mm, v(34.22, 57.22) * mm, v(29.28, 57.11) * mm, v(27.64, 56.82) * mm]});
            skFitSpline(sketch, "E267", {"points": [v(27.64, 56.82) * mm, v(24.32, 56.23) * mm, v(21.17, 55.04) * mm, v(18.35, 53.34) * mm]});
            skFitSpline(sketch, "E268", {"points": [v(18.35, 53.34) * mm, v(16.58, 52.26) * mm, v(13.88, 50.18) * mm, v(14.03, 50) * mm]});
            skFitSpline(sketch, "E269", {"points": [v(14.03, 50) * mm, v(14.1, 49.93) * mm, v(14.64, 49.7) * mm, v(15.25, 49.52) * mm]});
            skFitSpline(sketch, "E270", {"points": [v(15.25, 49.52) * mm, v(16.18, 49.22) * mm, v(16.7, 49.16) * mm, v(18.7, 49.16) * mm]});
            skFitSpline(sketch, "E271", {"points": [v(18.7, 49.16) * mm, v(21.26, 49.16) * mm, v(22.4, 49.38) * mm, v(24.83, 50.37) * mm]});
            skFitSpline(sketch, "E272", {"points": [v(24.83, 50.37) * mm, v(25.46, 50.63) * mm, v(26.02, 50.8) * mm, v(26.07, 50.74) * mm]});
            skFitSpline(sketch, "E273", {"points": [v(26.07, 50.74) * mm, v(26.4, 50.37) * mm, v(24.66, 49.2) * mm, v(22.68, 48.44) * mm]});
            skFitSpline(sketch, "E274", {"points": [v(22.68, 48.44) * mm, v(20.1, 47.45) * mm, v(15.95, 47) * mm, v(12.55, 47.32) * mm]});
            skFitSpline(sketch, "E275", {"points": [v(18.78, 47.86) * mm, v(19.58, 47.99) * mm, v(20.64, 48.2) * mm, v(21.13, 48.34) * mm]});
            skFitSpline(sketch, "E276", {"points": [v(21.13, 48.34) * mm, v(22.19, 48.65) * mm, v(24.06, 49.4) * mm, v(23.98, 49.49) * mm]});
            skFitSpline(sketch, "E277", {"points": [v(23.98, 49.49) * mm, v(23.95, 49.52) * mm, v(23.4, 49.4) * mm, v(22.76, 49.23) * mm]});
            skFitSpline(sketch, "E278", {"points": [v(22.76, 49.23) * mm, v(20.05, 48.48) * mm, v(17.32, 48.48) * mm, v(14.92, 49.23) * mm]});
            skFitSpline(sketch, "E279", {"points": [v(14.92, 49.23) * mm, v(13.56, 49.65) * mm, v(13.24, 49.88) * mm, v(13.5, 50.24) * mm]});
            skFitSpline(sketch, "E280", {"points": [v(13.5, 50.24) * mm, v(13.89, 50.77) * mm, v(16.98, 53.01) * mm, v(18.74, 54.03) * mm]});
            skFitSpline(sketch, "E281", {"points": [v(18.74, 54.03) * mm, v(22.73, 56.34) * mm, v(26.97, 57.48) * mm, v(31.72, 57.53) * mm]});
            skFitSpline(sketch, "E282", {"points": [v(32.73, 57.76) * mm, v(32.23, 57.88) * mm, v(31.02, 58.06) * mm, v(30.02, 58.16) * mm]});
            skFitSpline(sketch, "E283", {"points": [v(30.02, 58.16) * mm, v(23.26, 58.88) * mm, v(15.96, 55.7) * mm, v(10.55, 49.69) * mm]});
            skLineSegment(sketch, "E284", {"start": v(31.72, 57.53) * mm, "end": v(33.63, 57.55) * mm});
            skLineSegment(sketch, "E285", {"start": v(33.63, 57.55) * mm, "end": v(32.73, 57.76) * mm});
            skFitSpline(sketch, "E286", {"points": [v(10.55, 47.97) * mm, v(11.3, 47.87) * mm, v(12.11, 47.77) * mm, v(12.34, 47.74) * mm]});
            skFitSpline(sketch, "E287", {"points": [v(12.34, 47.74) * mm, v(13.46, 47.58) * mm, v(17.47, 47.66) * mm, v(18.78, 47.86) * mm]});
            skLineSegment(sketch, "E288", {"start": v(10.55, 49.69) * mm, "end": v(9.17, 48.15) * mm});
            skLineSegment(sketch, "E289", {"start": v(9.17, 48.15) * mm, "end": v(10.55, 47.97) * mm});
            skFitSpline(sketch, "E290", {"points": [v(-29, 51.51) * mm, v(-29.04, 51.64) * mm, v(-28.89, 52.16) * mm, v(-28.66, 52.67) * mm]});
            skFitSpline(sketch, "E291", {"points": [v(-28.66, 52.67) * mm, v(-28.44, 53.19) * mm, v(-28.15, 54) * mm, v(-28.03, 54.47) * mm]});
            skFitSpline(sketch, "E292", {"points": [v(-28.03, 54.47) * mm, v(-27.8, 55.4) * mm, v(-27.73, 56.71) * mm, v(-27.93, 56.71) * mm]});
            skFitSpline(sketch, "E293", {"points": [v(-27.93, 56.71) * mm, v(-27.99, 56.71) * mm, v(-28.57, 56.3) * mm, v(-29.2, 55.81) * mm]});
            skFitSpline(sketch, "E294", {"points": [v(-29.2, 55.81) * mm, v(-30.9, 54.5) * mm, v(-33.94, 52.89) * mm, v(-34.74, 52.89) * mm]});
            skFitSpline(sketch, "E295", {"points": [v(-34.74, 52.89) * mm, v(-35.06, 52.89) * mm, v(-35.06, 53.1) * mm, v(-34.72, 54.23) * mm]});
            skFitSpline(sketch, "E296", {"points": [v(-34.72, 54.23) * mm, v(-34.32, 55.58) * mm, v(-33.35, 57.04) * mm, v(-32.36, 57.8) * mm]});
            skFitSpline(sketch, "E297", {"points": [v(-32.36, 57.8) * mm, v(-30.94, 58.9) * mm, v(-30, 59.02) * mm, v(-27.2, 58.43) * mm]});
            skFitSpline(sketch, "E298", {"points": [v(-27.2, 58.43) * mm, v(-24.79, 57.93) * mm, v(-22.15, 57.94) * mm, v(-20.24, 58.45) * mm]});
            skFitSpline(sketch, "E299", {"points": [v(-20.24, 58.45) * mm, v(-19.46, 58.66) * mm, v(-18.78, 58.79) * mm, v(-18.73, 58.73) * mm]});
            skFitSpline(sketch, "E300", {"points": [v(-18.73, 58.73) * mm, v(-18.45, 58.4) * mm, v(-20.35, 56.02) * mm, v(-21.88, 54.76) * mm]});
            skFitSpline(sketch, "E301", {"points": [v(-21.88, 54.76) * mm, v(-23.08, 53.77) * mm, v(-25.05, 52.66) * mm, v(-26.75, 52.02) * mm]});
            skFitSpline(sketch, "E302", {"points": [v(-26.75, 52.02) * mm, v(-28.67, 51.3) * mm, v(-28.9, 51.24) * mm, v(-29, 51.51) * mm]});
            skFitSpline(sketch, "E303", {"points": [v(-27.08, 52.32) * mm, v(-25.15, 53.04) * mm, v(-23.2, 54.18) * mm, v(-21.8, 55.39) * mm]});
            skFitSpline(sketch, "E304", {"points": [v(-21.8, 55.39) * mm, v(-20.58, 56.45) * mm, v(-18.96, 58.43) * mm, v(-19.46, 58.24) * mm]});
            skFitSpline(sketch, "E305", {"points": [v(-19.46, 58.24) * mm, v(-21.25, 57.6) * mm, v(-24.35, 57.5) * mm, v(-26.9, 58) * mm]});
            skFitSpline(sketch, "E306", {"points": [v(-26.9, 58) * mm, v(-29.18, 58.47) * mm, v(-30.45, 58.47) * mm, v(-31.32, 58.02) * mm]});
            skFitSpline(sketch, "E307", {"points": [v(-31.32, 58.02) * mm, v(-32.26, 57.53) * mm, v(-33.08, 56.72) * mm, v(-33.64, 55.72) * mm]});
            skFitSpline(sketch, "E308", {"points": [v(-33.64, 55.72) * mm, v(-34.16, 54.81) * mm, v(-34.64, 53.54) * mm, v(-34.52, 53.4) * mm]});
            skFitSpline(sketch, "E309", {"points": [v(-34.52, 53.4) * mm, v(-34.39, 53.25) * mm, v(-31.9, 54.46) * mm, v(-30.64, 55.3) * mm]});
            skFitSpline(sketch, "E310", {"points": [v(-30.64, 55.3) * mm, v(-29.97, 55.74) * mm, v(-29.1, 56.38) * mm, v(-28.7, 56.72) * mm]});
            skFitSpline(sketch, "E311", {"points": [v(-28.7, 56.72) * mm, v(-28.29, 57.07) * mm, v(-27.9, 57.35) * mm, v(-27.82, 57.35) * mm]});
            skFitSpline(sketch, "E312", {"points": [v(-27.82, 57.35) * mm, v(-27.75, 57.35) * mm, v(-27.62, 57.09) * mm, v(-27.52, 56.77) * mm]});
            skFitSpline(sketch, "E313", {"points": [v(-27.52, 56.77) * mm, v(-27.3, 55.96) * mm, v(-27.56, 54.35) * mm, v(-28.16, 52.9) * mm]});
            skFitSpline(sketch, "E314", {"points": [v(-28.16, 52.9) * mm, v(-28.42, 52.28) * mm, v(-28.6, 51.77) * mm, v(-28.57, 51.77) * mm]});
            skFitSpline(sketch, "E315", {"points": [v(-28.57, 51.77) * mm, v(-28.54, 51.77) * mm, v(-27.87, 52.02) * mm, v(-27.08, 52.32) * mm]});
            skFitSpline(sketch, "E316", {"points": [v(-23.18, 22.32) * mm, v(-22.5, 26.09) * mm, v(-22.39, 30.09) * mm, v(-22.9, 33.36) * mm]});
            skFitSpline(sketch, "E317", {"points": [v(-22.9, 33.36) * mm, v(-23.02, 34.14) * mm, v(-23.07, 34.84) * mm, v(-23, 34.91) * mm]});
            skFitSpline(sketch, "E318", {"points": [v(-23, 34.91) * mm, v(-22.77, 35.19) * mm, v(-18.49, 33.68) * mm, v(-15.56, 32.3) * mm]});
            skFitSpline(sketch, "E319", {"points": [v(-15.56, 32.3) * mm, v(-12.06, 30.64) * mm, v(-7.35, 27.56) * mm, v(-4.8, 25.27) * mm]});
            skFitSpline(sketch, "E320", {"points": [v(-4.8, 25.27) * mm, v(-4.5, 25) * mm, v(-4.3, 24.86) * mm, v(-4.36, 24.97) * mm]});
            skFitSpline(sketch, "E321", {"points": [v(-4.36, 24.97) * mm, v(-4.57, 25.37) * mm, v(-7.36, 27.84) * mm, v(-9.01, 29.08) * mm]});
            skFitSpline(sketch, "E322", {"points": [v(-9.01, 29.08) * mm, v(-13.46, 32.44) * mm, v(-18.87, 35.39) * mm, v(-22.75, 36.57) * mm]});
            skFitSpline(sketch, "E323", {"points": [v(-22.75, 36.57) * mm, v(-23.48, 36.8) * mm, v(-23.72, 36.94) * mm, v(-23.78, 37.19) * mm]});
            skFitSpline(sketch, "E324", {"points": [v(-23.78, 37.19) * mm, v(-23.82, 37.37) * mm, v(-24.18, 38.28) * mm, v(-24.58, 39.21) * mm]});
            skFitSpline(sketch, "E325", {"points": [v(-24.58, 39.21) * mm, v(-24.99, 40.15) * mm, v(-25.32, 40.98) * mm, v(-25.32, 41.07) * mm]});
            skFitSpline(sketch, "E326", {"points": [v(-25.32, 41.07) * mm, v(-25.32, 41.33) * mm, v(-24.37, 41.42) * mm, v(-21.45, 41.42) * mm]});
            skFitSpline(sketch, "E327", {"points": [v(-21.45, 41.42) * mm, v(-15.9, 41.42) * mm, v(-10.71, 40.43) * mm, v(-5.24, 38.33) * mm]});
            skFitSpline(sketch, "E328", {"points": [v(-5.24, 38.33) * mm, v(-4.04, 37.87) * mm, v(-3.11, 37.54) * mm, v(-3.17, 37.6) * mm]});
            skFitSpline(sketch, "E329", {"points": [v(-3.17, 37.6) * mm, v(-3.45, 37.87) * mm, v(-5.76, 38.95) * mm, v(-7.59, 39.68) * mm]});
            skFitSpline(sketch, "E330", {"points": [v(-7.59, 39.68) * mm, v(-13.02, 41.82) * mm, v(-19.04, 43.01) * mm, v(-24.43, 43.01) * mm]});
            skFitSpline(sketch, "E331", {"points": [v(-27.59, 43.95) * mm, v(-28.05, 44.47) * mm, v(-28.62, 45.07) * mm, v(-28.84, 45.3) * mm]});
            skFitSpline(sketch, "E332", {"points": [v(-28.84, 45.3) * mm, v(-29.13, 45.57) * mm, v(-29.22, 45.75) * mm, v(-29.12, 45.87) * mm]});
            skFitSpline(sketch, "E333", {"points": [v(-29.12, 45.87) * mm, v(-28.9, 46.12) * mm, v(-24.88, 47.26) * mm, v(-22.66, 47.7) * mm]});
            skFitSpline(sketch, "E334", {"points": [v(-22.66, 47.7) * mm, v(-16.7, 48.87) * mm, v(-10.13, 49.02) * mm, v(-4.04, 48.12) * mm]});
            skFitSpline(sketch, "E335", {"points": [v(-4.04, 48.12) * mm, v(-2.93, 47.96) * mm, v(-2.01, 47.85) * mm, v(-1.99, 47.87) * mm]});
            skFitSpline(sketch, "E336", {"points": [v(-1.99, 47.87) * mm, v(-1.89, 47.98) * mm, v(-5.1, 48.76) * mm, v(-6.87, 49.05) * mm]});
            skFitSpline(sketch, "E337", {"points": [v(-6.87, 49.05) * mm, v(-9.74, 49.52) * mm, v(-12.16, 49.7) * mm, v(-15.64, 49.7) * mm]});
            skFitSpline(sketch, "E338", {"points": [v(-15.64, 49.7) * mm, v(-21.34, 49.7) * mm, v(-25.53, 49.15) * mm, v(-30.17, 47.77) * mm]});
            skLineSegment(sketch, "E339", {"start": v(-24.43, 43.01) * mm, "end": v(-26.74, 43.01) * mm});
            skLineSegment(sketch, "E340", {"start": v(-26.74, 43.01) * mm, "end": v(-27.59, 43.95) * mm});
            skFitSpline(sketch, "E341", {"points": [v(-32.8, 47.77) * mm, v(-33.93, 48.28) * mm, v(-35.68, 48.8) * mm, v(-37.1, 49.07) * mm]});
            skLineSegment(sketch, "E342", {"start": v(-30.17, 47.77) * mm, "end": v(-31.78, 47.3) * mm});
            skLineSegment(sketch, "E343", {"start": v(-31.78, 47.3) * mm, "end": v(-32.8, 47.77) * mm});
            skFitSpline(sketch, "E344", {"points": [v(-40.87, 46.88) * mm, v(-32.76, 46.3) * mm, v(-26.28, 40.58) * mm, v(-24.17, 32.17) * mm]});
            skFitSpline(sketch, "E345", {"points": [v(-24.17, 32.17) * mm, v(-23.53, 29.62) * mm, v(-23.34, 27.65) * mm, v(-23.43, 24.3) * mm]});
            skFitSpline(sketch, "E346", {"points": [v(-23.43, 24.3) * mm, v(-23.48, 22.63) * mm, v(-23.56, 21.05) * mm, v(-23.6, 20.8) * mm]});
            skFitSpline(sketch, "E347", {"points": [v(-23.6, 20.8) * mm, v(-23.66, 20.53) * mm, v(-23.66, 20.36) * mm, v(-23.6, 20.41) * mm]});
            skFitSpline(sketch, "E348", {"points": [v(-23.6, 20.41) * mm, v(-23.56, 20.47) * mm, v(-23.36, 21.33) * mm, v(-23.18, 22.32) * mm]});
            skLineSegment(sketch, "E349", {"start": v(-37.1, 49.07) * mm, "end": v(-38.05, 49.23) * mm});
            skLineSegment(sketch, "E350", {"start": v(-38.05, 49.23) * mm, "end": v(-39.73, 48.07) * mm});
            skLineSegment(sketch, "E351", {"start": v(-39.73, 48.07) * mm, "end": v(-41.41, 46.92) * mm});
            skLineSegment(sketch, "E352", {"start": v(-41.41, 46.92) * mm, "end": v(-40.87, 46.88) * mm});
            skFitSpline(sketch, "E353", {"points": [v(-3.07, 23.63) * mm, v(-3.07, 23.66) * mm, v(-3.2, 23.83) * mm, v(-3.38, 24) * mm]});
            skFitSpline(sketch, "E354", {"points": [v(-3.43, 23.94) * mm, v(-3.18, 23.6) * mm, v(-3.07, 23.5) * mm, v(-3.07, 23.63) * mm]});
            skLineSegment(sketch, "E355", {"start": v(-3.38, 24) * mm, "end": v(-3.7, 24.3) * mm});
            skLineSegment(sketch, "E356", {"start": v(-3.7, 24.3) * mm, "end": v(-3.43, 23.94) * mm});
            skFitSpline(sketch, "E357", {"points": [v(-41.27, -5.88) * mm, v(-42.68, -4.46) * mm, v(-43.35, -1.24) * mm, v(-43.02, 2.56) * mm]});
            skFitSpline(sketch, "E358", {"points": [v(-43.02, 2.56) * mm, v(-42.78, 5.3) * mm, v(-42.12, 7.97) * mm, v(-41.69, 7.97) * mm]});
            skFitSpline(sketch, "E359", {"points": [v(-41.69, 7.97) * mm, v(-41.6, 7.97) * mm, v(-41.48, 7.63) * mm, v(-41.42, 7.21) * mm]});
            skFitSpline(sketch, "E360", {"points": [v(-41.42, 7.21) * mm, v(-41.13, 4.92) * mm, v(-39.94, 1.93) * mm, v(-38.8, 0.6) * mm]});
            skFitSpline(sketch, "E361", {"points": [v(-38.8, 0.6) * mm, v(-37.76, -0.63) * mm, v(-37, -1.02) * mm, v(-35.62, -1) * mm]});
            skFitSpline(sketch, "E362", {"points": [v(-35.62, -1) * mm, v(-33.12, -1) * mm, v(-30.25, 0.76) * mm, v(-27.24, 4.1) * mm]});
            skFitSpline(sketch, "E363", {"points": [v(-27.24, 4.1) * mm, v(-26.59, 4.83) * mm, v(-25.98, 5.42) * mm, v(-25.88, 5.42) * mm]});
            skFitSpline(sketch, "E364", {"points": [v(-25.88, 5.42) * mm, v(-25.5, 5.42) * mm, v(-26.28, 3.62) * mm, v(-27.37, 2.04) * mm]});
            skFitSpline(sketch, "E365", {"points": [v(-27.37, 2.04) * mm, v(-29.66, -1.27) * mm, v(-33.85, -4.1) * mm, v(-39.04, -5.82) * mm]});
            skFitSpline(sketch, "E366", {"points": [v(-39.04, -5.82) * mm, v(-39.94, -6.12) * mm, v(-40.7, -6.37) * mm, v(-40.74, -6.37) * mm]});
            skFitSpline(sketch, "E367", {"points": [v(-40.74, -6.37) * mm, v(-40.77, -6.37) * mm, v(-41, -6.15) * mm, v(-41.27, -5.88) * mm]});
            skFitSpline(sketch, "E368", {"points": [v(-39.12, -5.41) * mm, v(-34.27, -3.8) * mm, v(-30.2, -1.12) * mm, v(-27.89, 2.02) * mm]});
            skFitSpline(sketch, "E369", {"points": [v(-27.89, 2.02) * mm, v(-27.43, 2.64) * mm, v(-26.93, 3.4) * mm, v(-26.78, 3.7) * mm]});
            skFitSpline(sketch, "E370", {"points": [v(-26.78, 3.7) * mm, v(-26.54, 4.16) * mm, v(-26.61, 4.12) * mm, v(-27.36, 3.32) * mm]});
            skFitSpline(sketch, "E371", {"points": [v(-27.36, 3.32) * mm, v(-29.22, 1.35) * mm, v(-31.03, 0) * mm, v(-32.93, -0.82) * mm]});
            skFitSpline(sketch, "E372", {"points": [v(-32.93, -0.82) * mm, v(-33.96, -1.27) * mm, v(-34.27, -1.33) * mm, v(-35.55, -1.34) * mm]});
            skFitSpline(sketch, "E373", {"points": [v(-35.55, -1.34) * mm, v(-36.83, -1.35) * mm, v(-37.08, -1.3) * mm, v(-37.67, -0.95) * mm]});
            skFitSpline(sketch, "E374", {"points": [v(-37.67, -0.95) * mm, v(-38.8, -0.29) * mm, v(-39.76, 0.97) * mm, v(-40.53, 2.78) * mm]});
            skFitSpline(sketch, "E375", {"points": [v(-40.53, 2.78) * mm, v(-40.9, 3.66) * mm, v(-41.34, 4.95) * mm, v(-41.49, 5.65) * mm]});
            skFitSpline(sketch, "E376", {"points": [v(-41.49, 5.65) * mm, v(-41.64, 6.34) * mm, v(-41.8, 6.94) * mm, v(-41.82, 6.97) * mm]});
            skFitSpline(sketch, "E377", {"points": [v(-41.82, 6.97) * mm, v(-41.85, 7) * mm, v(-41.98, 6.66) * mm, v(-42.1, 6.19) * mm]});
            skFitSpline(sketch, "E378", {"points": [v(-42.1, 6.19) * mm, v(-42.98, 2.65) * mm, v(-42.93, -1.8) * mm, v(-41.97, -4.02) * mm]});
            skFitSpline(sketch, "E379", {"points": [v(-41.97, -4.02) * mm, v(-41.64, -4.8) * mm, v(-40.86, -5.89) * mm, v(-40.65, -5.89) * mm]});
            skFitSpline(sketch, "E380", {"points": [v(-40.65, -5.89) * mm, v(-40.6, -5.89) * mm, v(-39.92, -5.68) * mm, v(-39.12, -5.41) * mm]});
            skFitSpline(sketch, "E381", {"points": [v(-46.69, 13) * mm, v(-50.18, 15.52) * mm, v(-52.5, 18.17) * mm, v(-53.93, 21.24) * mm]});
            skFitSpline(sketch, "E382", {"points": [v(-53.93, 21.24) * mm, v(-54.22, 21.87) * mm, v(-54.57, 22.8) * mm, v(-54.7, 23.32) * mm]});
            skFitSpline(sketch, "E383", {"points": [v(-54.35, 24.88) * mm, v(-53.19, 26.07) * mm, v(-51.04, 27.01) * mm, v(-48.55, 27.42) * mm]});
            skFitSpline(sketch, "E384", {"points": [v(-48.55, 27.42) * mm, v(-46.83, 27.7) * mm, v(-43.96, 27.52) * mm, v(-42.31, 27.03) * mm]});
            skFitSpline(sketch, "E385", {"points": [v(-42.31, 27.03) * mm, v(-37.92, 25.73) * mm, v(-34.1, 22.47) * mm, v(-32.34, 18.53) * mm]});
            skFitSpline(sketch, "E386", {"points": [v(-32.34, 18.53) * mm, v(-31.85, 17.46) * mm, v(-31.78, 17.18) * mm, v(-31.93, 17.02) * mm]});
            skFitSpline(sketch, "E387", {"points": [v(-31.93, 17.02) * mm, v(-32.08, 16.85) * mm, v(-32.14, 16.87) * mm, v(-32.27, 17.13) * mm]});
            skFitSpline(sketch, "E388", {"points": [v(-32.27, 17.13) * mm, v(-32.8, 18.22) * mm, v(-35.25, 20.55) * mm, v(-37.28, 21.89) * mm]});
            skFitSpline(sketch, "E389", {"points": [v(-37.28, 21.89) * mm, v(-39.61, 23.44) * mm, v(-42.42, 24.46) * mm, v(-44.83, 24.64) * mm]});
            skFitSpline(sketch, "E390", {"points": [v(-44.83, 24.64) * mm, v(-46.2, 24.74) * mm, v(-46.2, 24.74) * mm, v(-46.6, 24.3) * mm]});
            skFitSpline(sketch, "E391", {"points": [v(-46.6, 24.3) * mm, v(-48.25, 22.48) * mm, v(-47.8, 17.16) * mm, v(-45.7, 13.48) * mm]});
            skFitSpline(sketch, "E392", {"points": [v(-45.7, 13.48) * mm, v(-45.37, 12.87) * mm, v(-45.08, 12.32) * mm, v(-45.08, 12.25) * mm]});
            skFitSpline(sketch, "E393", {"points": [v(-45.08, 12.25) * mm, v(-45.08, 11.95) * mm, v(-45.51, 12.15) * mm, v(-46.69, 13) * mm]});
            skLineSegment(sketch, "E394", {"start": v(-54.7, 23.32) * mm, "end": v(-54.96, 24.26) * mm});
            skLineSegment(sketch, "E395", {"start": v(-54.96, 24.26) * mm, "end": v(-54.35, 24.88) * mm});
            skFitSpline(sketch, "E396", {"points": [v(-46.45, 14.05) * mm, v(-48.26, 17.78) * mm, v(-48.48, 22.7) * mm, v(-46.92, 24.57) * mm]});
            skFitSpline(sketch, "E397", {"points": [v(-46.92, 24.57) * mm, v(-46.57, 25) * mm, v(-46.5, 25.01) * mm, v(-45.25, 25.01) * mm]});
            skFitSpline(sketch, "E398", {"points": [v(-45.25, 25.01) * mm, v(-41.4, 25.01) * mm, v(-37.16, 22.94) * mm, v(-33.34, 19.17) * mm]});
            skFitSpline(sketch, "E399", {"points": [v(-33, 19.1) * mm, v(-33.77, 20.62) * mm, v(-35.59, 22.7) * mm, v(-37.3, 24.04) * mm]});
            skFitSpline(sketch, "E400", {"points": [v(-37.3, 24.04) * mm, v(-41.74, 27.5) * mm, v(-48.18, 28.17) * mm, v(-52.62, 25.64) * mm]});
            skFitSpline(sketch, "E401", {"points": [v(-52.62, 25.64) * mm, v(-53.87, 24.92) * mm, v(-54.48, 24.36) * mm, v(-54.48, 23.95) * mm]});
            skFitSpline(sketch, "E402", {"points": [v(-54.48, 23.95) * mm, v(-54.48, 23.46) * mm, v(-53.59, 21.28) * mm, v(-52.91, 20.1) * mm]});
            skFitSpline(sketch, "E403", {"points": [v(-52.91, 20.1) * mm, v(-52.12, 18.73) * mm, v(-50.61, 16.85) * mm, v(-49.45, 15.78) * mm]});
            skFitSpline(sketch, "E404", {"points": [v(-49.45, 15.78) * mm, v(-48.35, 14.78) * mm, v(-46.16, 13.05) * mm, v(-46.09, 13.13) * mm]});
            skFitSpline(sketch, "E405", {"points": [v(-46.09, 13.13) * mm, v(-46.06, 13.17) * mm, v(-46.22, 13.58) * mm, v(-46.45, 14.05) * mm]});
            skLineSegment(sketch, "E406", {"start": v(-33.34, 19.17) * mm, "end": v(-32.73, 18.56) * mm});
            skLineSegment(sketch, "E407", {"start": v(-32.73, 18.56) * mm, "end": v(-33, 19.1) * mm});
            skLineSegment(sketch, "E408.bottom", {"start": v(-86.46, 86.62) * mm, "end": v(87.92, 86.62) * mm});
            skLineSegment(sketch, "E408.top", {"start": v(-86.46, -87) * mm, "end": v(87.92, -87) * mm});
            skLineSegment(sketch, "E408.left", {"start": v(-86.46, 86.62) * mm, "end": v(-86.46, -87) * mm});
            skLineSegment(sketch, "E408.right", {"start": v(87.92, 86.62) * mm, "end": v(87.92, -87) * mm});
            skSolve(sketch);
        }
        {
            var Q0;
            Q0=makeQuery(id+"F0.imprint","IMPRINT",FACE,{"disambiguationData":[TD([[makeQuery(id+"F0.imprint","IMPRINT",EDGE,{"derivedFrom":sQuery(id+"F0.wireOp",EDGE,"E316")}),1.0]])]});
            var Q1;
            Q1=makeQuery(id+"F0.imprint","IMPRINT",FACE,{"disambiguationData":[TD([[makeQuery(id+"F0.imprint","IMPRINT",EDGE,{"derivedFrom":sQuery(id+"F0.wireOp",EDGE,"E102")}),1.0]])]});
            var Q2;
            Q2=makeQuery(id+"F0.imprint","IMPRINT",FACE,{"disambiguationData":[TD([[makeQuery(id+"F0.imprint","IMPRINT",EDGE,{"derivedFrom":sQuery(id+"F0.wireOp",EDGE,"E396")}),1.0]])]});
            var Q3;
            Q3=makeQuery(id+"F0.imprint","IMPRINT",FACE,{"disambiguationData":[TD([[makeQuery(id+"F0.imprint","IMPRINT",EDGE,{"derivedFrom":sQuery(id+"F0.wireOp",EDGE,"E368")}),1.0]])]});
            extrude(context, id + "F1", {"entities" : qUnion([Q0, Q1, Q2, Q3]), "depth" : 10 * mm, "offsetDistance" : 25 * mm});
        }
    });
